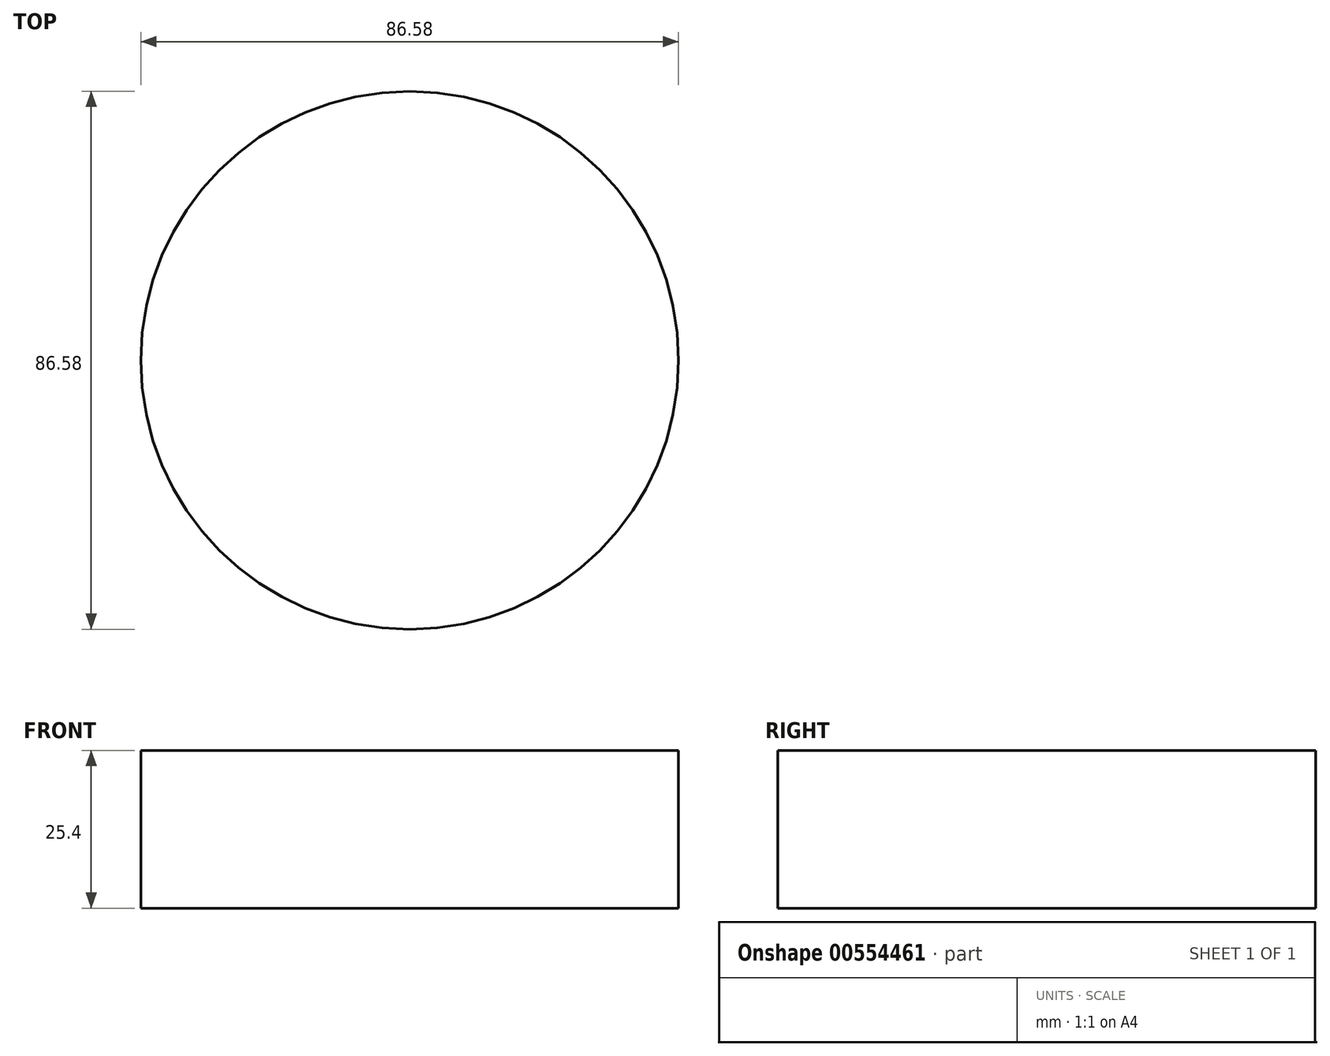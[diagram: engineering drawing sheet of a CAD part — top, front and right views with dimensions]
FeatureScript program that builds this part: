
annotation { "Feature Type Name" : "Feature", "Feature Type Description" : "" }
export const myFeature = defineFeature(function(context is Context, id is Id, definition is map)
    precondition{}
    {
        {
            var Q0;
            Q0=qCreatedBy(makeId("Top.planeOp"),FACE);
            var sketch = newSketch(context, id + "F0", { "sketchPlane" : qUnion([Q0])});
            skCircle(sketch, "E0", {"center": v(0, 0) * mm, "radius": 43.3 * mm});
            skSolve(sketch);
        }
        {
            var Q0;
            Q0=makeQuery(id+"F0.imprint","IMPRINT",FACE,{"disambiguationData":[TD([[makeQuery(id+"F0.imprint","IMPRINT",EDGE,{"derivedFrom":sQuery(id+"F0.wireOp",EDGE,"E0")}),1.0]])]});
            extrude(context, id + "F1", {"entities" : qUnion([Q0]), "depth" : 25.4 * mm, "offsetDistance" : 25.4 * mm});
        }
    });
